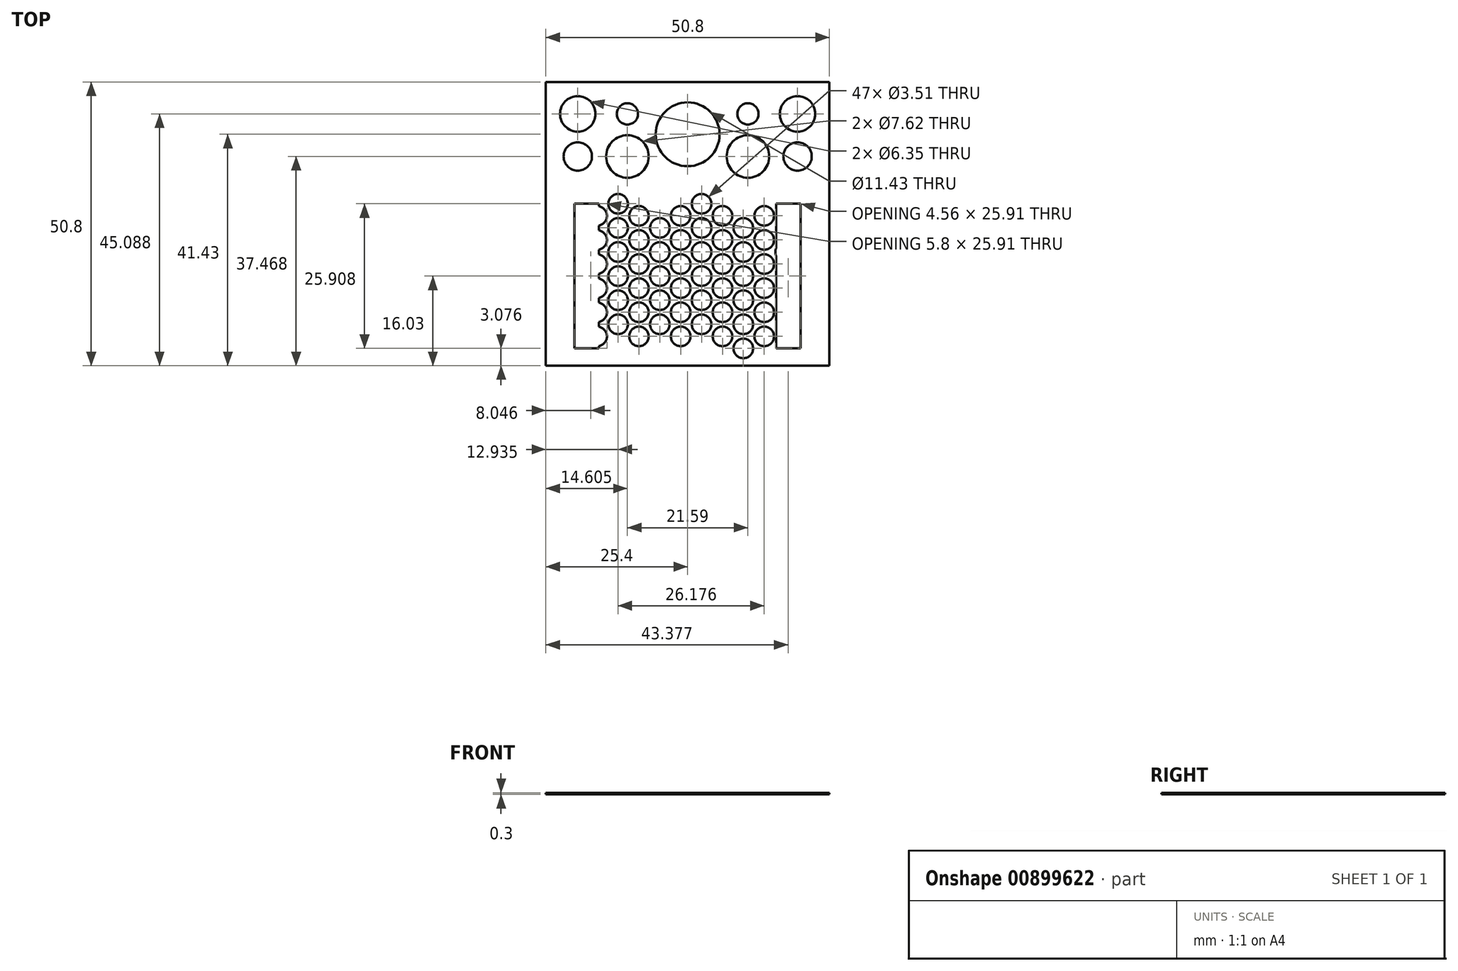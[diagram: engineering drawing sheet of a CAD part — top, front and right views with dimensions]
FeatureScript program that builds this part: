
annotation { "Feature Type Name" : "Feature", "Feature Type Description" : "" }
export const myFeature = defineFeature(function(context is Context, id is Id, definition is map)
    precondition{}
    {
        {
            var Q0;
            Q0=qCreatedBy(makeId("Top.planeOp"),FACE);
            var sketch = newSketch(context, id + "F0", { "sketchPlane" : qUnion([Q0])});
            skLineSegment(sketch, "E0.bottom", {"start": v(-25.4, -16.03) * mm, "end": v(25.4, -16.03) * mm});
            skLineSegment(sketch, "E0.top", {"start": v(-25.4, 34.77) * mm, "end": v(25.4, 34.77) * mm});
            skLineSegment(sketch, "E0.left", {"start": v(-25.4, -16.03) * mm, "end": v(-25.4, 34.77) * mm});
            skLineSegment(sketch, "E0.right", {"start": v(25.4, -16.03) * mm, "end": v(25.4, 34.77) * mm});
            skLineSegment(sketch, "E1.bottom", {"start": v(-20.26, -12.95) * mm, "end": v(20.26, -12.95) * mm});
            skLineSegment(sketch, "E1.top", {"start": v(-20.26, 12.95) * mm, "end": v(20.26, 12.95) * mm});
            skLineSegment(sketch, "E1.left", {"start": v(-20.26, -12.95) * mm, "end": v(-20.26, 12.95) * mm});
            skLineSegment(sketch, "E1.right", {"start": v(20.26, -12.95) * mm, "end": v(20.26, 12.95) * mm});
            skLineSegment(sketch, "E2", {"start": v(-15.88, 12.95) * mm, "end": v(-15.88, -12.95) * mm});
            skLineSegment(sketch, "E3", {"start": v(-20.26, -12.95) * mm, "end": v(20.26, 12.95) * mm, "construction": true});
            skLineSegment(sketch, "E4", {"start": v(15.88, -12.95) * mm, "end": v(15.88, 12.95) * mm});
            skCircle(sketch, "E5", {"center": v(-12.46, -8.64) * mm, "radius": 1.75 * mm});
            skCircle(sketch, "E6.cCircle", {"center": v(-12.46, -8.64) * mm, "radius": 3.74 * mm, "construction": true});
            skLineSegment(sketch, "E6.0", {"start": v(-8.73, -10.8) * mm, "end": v(-8.73, -6.48) * mm, "construction": true});
            skLineSegment(sketch, "E6.1", {"start": v(-12.46, -12.95) * mm, "end": v(-8.73, -10.8) * mm, "construction": true});
            skLineSegment(sketch, "E6.2", {"start": v(-16.2, -10.8) * mm, "end": v(-12.46, -12.95) * mm, "construction": true});
            skLineSegment(sketch, "E6.3", {"start": v(-16.2, -6.48) * mm, "end": v(-16.2, -10.8) * mm, "construction": true});
            skLineSegment(sketch, "E6.4", {"start": v(-12.46, -4.32) * mm, "end": v(-16.2, -6.48) * mm, "construction": true});
            skLineSegment(sketch, "E6.5", {"start": v(-8.73, -6.48) * mm, "end": v(-12.46, -4.32) * mm, "construction": true});
            skPoint(sketch, "E6.0.midPoint", {"position": v(-8.73, -8.64) * mm});
            skCircle(sketch, "E7", {"center": v(-16.2, -10.8) * mm, "radius": 1.75 * mm});
            skCircle(sketch, "E8", {"center": v(-16.2, -6.48) * mm, "radius": 1.75 * mm});
            skCircle(sketch, "E9", {"center": v(-12.46, -4.32) * mm, "radius": 1.75 * mm});
            skCircle(sketch, "E10.0.1.0", {"center": v(-16.2, -2.16) * mm, "radius": 1.75 * mm});
            skCircle(sketch, "E10.0.1.1", {"center": v(-12.46, 4.32) * mm, "radius": 1.75 * mm});
            skCircle(sketch, "E10.0.1.2", {"center": v(-16.2, 2.16) * mm, "radius": 1.75 * mm});
            skCircle(sketch, "E10.0.1.3", {"center": v(-12.46, 0) * mm, "radius": 1.75 * mm});
            skCircle(sketch, "E10.0.2.0", {"center": v(-16.2, 6.48) * mm, "radius": 1.75 * mm});
            skCircle(sketch, "E10.0.2.1", {"center": v(-12.46, 12.95) * mm, "radius": 1.75 * mm});
            skCircle(sketch, "E10.0.2.2", {"center": v(-16.2, 10.8) * mm, "radius": 1.75 * mm});
            skCircle(sketch, "E10.0.2.3", {"center": v(-12.46, 8.64) * mm, "radius": 1.75 * mm});
            skCircle(sketch, "E10.1.0.0", {"center": v(-8.73, -10.8) * mm, "radius": 1.75 * mm});
            skCircle(sketch, "E10.1.0.1", {"center": v(-4.99, -4.32) * mm, "radius": 1.75 * mm});
            skCircle(sketch, "E10.1.0.2", {"center": v(-8.73, -6.48) * mm, "radius": 1.75 * mm});
            skCircle(sketch, "E10.1.0.3", {"center": v(-4.99, -8.64) * mm, "radius": 1.75 * mm});
            skCircle(sketch, "E10.1.1.0", {"center": v(-8.73, -2.16) * mm, "radius": 1.75 * mm});
            skCircle(sketch, "E10.1.1.1", {"center": v(-4.99, 4.32) * mm, "radius": 1.75 * mm});
            skCircle(sketch, "E10.1.1.2", {"center": v(-8.73, 2.16) * mm, "radius": 1.75 * mm});
            skCircle(sketch, "E10.1.1.3", {"center": v(-4.99, 0) * mm, "radius": 1.75 * mm});
            skCircle(sketch, "E10.1.2.0", {"center": v(-8.73, 6.48) * mm, "radius": 1.75 * mm});
            skCircle(sketch, "E10.1.2.1", {"center": v(-4.99, 12.95) * mm, "radius": 1.75 * mm});
            skCircle(sketch, "E10.1.2.2", {"center": v(-8.73, 10.8) * mm, "radius": 1.75 * mm});
            skCircle(sketch, "E10.1.2.3", {"center": v(-4.99, 8.64) * mm, "radius": 1.75 * mm});
            skCircle(sketch, "E10.2.0.0", {"center": v(-1.25, -10.8) * mm, "radius": 1.75 * mm});
            skCircle(sketch, "E10.2.0.1", {"center": v(2.5, -4.32) * mm, "radius": 1.75 * mm});
            skCircle(sketch, "E10.2.0.2", {"center": v(-1.25, -6.48) * mm, "radius": 1.75 * mm});
            skCircle(sketch, "E10.2.0.3", {"center": v(2.5, -8.64) * mm, "radius": 1.75 * mm});
            skCircle(sketch, "E10.2.1.0", {"center": v(-1.25, -2.16) * mm, "radius": 1.75 * mm});
            skCircle(sketch, "E10.2.1.1", {"center": v(2.5, 4.32) * mm, "radius": 1.75 * mm});
            skCircle(sketch, "E10.2.1.2", {"center": v(-1.25, 2.16) * mm, "radius": 1.75 * mm});
            skCircle(sketch, "E10.2.1.3", {"center": v(2.5, 0) * mm, "radius": 1.75 * mm});
            skCircle(sketch, "E10.2.2.0", {"center": v(-1.25, 6.48) * mm, "radius": 1.75 * mm});
            skCircle(sketch, "E10.2.2.1", {"center": v(2.5, 12.95) * mm, "radius": 1.75 * mm});
            skCircle(sketch, "E10.2.2.2", {"center": v(-1.25, 10.8) * mm, "radius": 1.75 * mm});
            skCircle(sketch, "E10.2.2.3", {"center": v(2.5, 8.64) * mm, "radius": 1.75 * mm});
            skCircle(sketch, "E10.3.0.0", {"center": v(6.23, -10.8) * mm, "radius": 1.75 * mm});
            skCircle(sketch, "E10.3.0.1", {"center": v(9.97, -4.32) * mm, "radius": 1.75 * mm});
            skCircle(sketch, "E10.3.0.2", {"center": v(6.23, -6.48) * mm, "radius": 1.75 * mm});
            skCircle(sketch, "E10.3.0.3", {"center": v(9.97, -8.64) * mm, "radius": 1.75 * mm});
            skCircle(sketch, "E10.3.1.0", {"center": v(6.23, -2.16) * mm, "radius": 1.75 * mm});
            skCircle(sketch, "E10.3.1.1", {"center": v(9.97, 4.32) * mm, "radius": 1.75 * mm});
            skCircle(sketch, "E10.3.1.2", {"center": v(6.23, 2.16) * mm, "radius": 1.75 * mm});
            skCircle(sketch, "E10.3.1.3", {"center": v(9.97, 0) * mm, "radius": 1.75 * mm});
            skCircle(sketch, "E10.3.2.0", {"center": v(6.23, 6.48) * mm, "radius": 1.75 * mm});
            skCircle(sketch, "E10.3.2.1", {"center": v(9.97, 12.95) * mm, "radius": 1.75 * mm});
            skCircle(sketch, "E10.3.2.2", {"center": v(6.23, 10.8) * mm, "radius": 1.75 * mm});
            skCircle(sketch, "E10.3.2.3", {"center": v(9.97, 8.64) * mm, "radius": 1.75 * mm});
            skLineSegment(sketch, "E10.direction1", {"start": v(-16.2, -10.8) * mm, "end": v(-8.73, -10.8) * mm, "construction": true});
            skLineSegment(sketch, "E10.direction2", {"start": v(-16.2, -10.8) * mm, "end": v(-16.2, -2.16) * mm, "construction": true});
            skLineSegment(sketch, "E11", {"start": v(-8.73, -6.48) * mm, "end": v(-8.73, -2.16) * mm, "construction": true});
            skLineSegment(sketch, "E12", {"start": v(-1.25, 2.16) * mm, "end": v(0, 0) * mm, "construction": true});
            skLineSegment(sketch, "E13", {"start": v(0, 0) * mm, "end": v(2.5, 0) * mm, "construction": true});
            skLineSegment(sketch, "E14", {"start": v(-1.25, -2.16) * mm, "end": v(0, 0) * mm, "construction": true});
            skCircle(sketch, "E15.0.4.0", {"center": v(13.71, -10.8) * mm, "radius": 1.75 * mm});
            skCircle(sketch, "E15.2.4.0", {"center": v(17.45, -4.32) * mm, "radius": 1.75 * mm});
            skCircle(sketch, "E15.4.4.0", {"center": v(13.71, -6.48) * mm, "radius": 1.75 * mm});
            skCircle(sketch, "E15.6.4.0", {"center": v(17.45, -8.64) * mm, "radius": 1.75 * mm});
            skCircle(sketch, "E15.0.4.1", {"center": v(13.71, -2.16) * mm, "radius": 1.75 * mm});
            skCircle(sketch, "E15.2.4.1", {"center": v(17.45, 4.32) * mm, "radius": 1.75 * mm});
            skCircle(sketch, "E15.4.4.1", {"center": v(13.71, 2.16) * mm, "radius": 1.75 * mm});
            skCircle(sketch, "E15.6.4.1", {"center": v(17.45, 0) * mm, "radius": 1.75 * mm});
            skCircle(sketch, "E15.0.4.2", {"center": v(13.71, 6.48) * mm, "radius": 1.75 * mm});
            skCircle(sketch, "E15.2.4.2", {"center": v(17.45, 12.95) * mm, "radius": 1.75 * mm});
            skCircle(sketch, "E15.4.4.2", {"center": v(13.71, 10.8) * mm, "radius": 1.75 * mm});
            skCircle(sketch, "E15.6.4.2", {"center": v(17.45, 8.64) * mm, "radius": 1.75 * mm});
            skCircle(sketch, "E16", {"center": v(-12.46, -12.95) * mm, "radius": 1.75 * mm});
            skCircle(sketch, "E17.1.0.0", {"center": v(-4.99, -12.95) * mm, "radius": 1.75 * mm});
            skCircle(sketch, "E17.2.0.0", {"center": v(2.5, -12.95) * mm, "radius": 1.75 * mm});
            skCircle(sketch, "E17.3.0.0", {"center": v(9.97, -12.95) * mm, "radius": 1.75 * mm});
            skLineSegment(sketch, "E17.direction1", {"start": v(-12.46, -12.95) * mm, "end": v(-4.99, -12.95) * mm, "construction": true});
            skLineSegment(sketch, "E18", {"start": v(-8.73, -10.8) * mm, "end": v(-4.99, -12.95) * mm, "construction": true});
            skLineSegment(sketch, "E19", {"start": v(-25.4, 16.03) * mm, "end": v(25.4, 16.03) * mm, "construction": true});
            skLineSegment(sketch, "E20", {"start": v(0, -16.03) * mm, "end": v(0, 0) * mm, "construction": true});
            skCircle(sketch, "E21.MirrorC", {"center": v(16.2, 6.48) * mm, "radius": 1.75 * mm, "construction": true});
            skCircle(sketch, "E22.MirrorC", {"center": v(-13.71, 6.48) * mm, "radius": 1.75 * mm, "construction": true});
            skCircle(sketch, "E23.MirrorC", {"center": v(12.46, 8.64) * mm, "radius": 1.75 * mm, "construction": true});
            skCircle(sketch, "E24.MirrorC", {"center": v(16.2, 10.8) * mm, "radius": 1.75 * mm, "construction": true});
            skCircle(sketch, "E25", {"center": v(0, 25.4) * mm, "radius": 5.72 * mm});
            skCircle(sketch, "E26", {"center": v(10.8, 21.44) * mm, "radius": 3.81 * mm});
            skCircle(sketch, "E27", {"center": v(19.69, 21.44) * mm, "radius": 2.54 * mm});
            skCircle(sketch, "E28", {"center": v(19.69, 29.06) * mm, "radius": 3.18 * mm});
            skCircle(sketch, "E29", {"center": v(10.8, 29.06) * mm, "radius": 1.9 * mm});
            skLineSegment(sketch, "E30", {"start": v(0, 16.03) * mm, "end": v(0, 34.77) * mm, "construction": true});
            skLineSegment(sketch, "E31", {"start": v(10.8, 29.06) * mm, "end": v(19.69, 29.06) * mm, "construction": true});
            skLineSegment(sketch, "E32", {"start": v(19.69, 29.06) * mm, "end": v(19.69, 21.44) * mm, "construction": true});
            skLineSegment(sketch, "E33", {"start": v(10.8, 29.06) * mm, "end": v(10.8, 21.44) * mm, "construction": true});
            skLineSegment(sketch, "E34", {"start": v(19.69, 21.44) * mm, "end": v(10.8, 21.44) * mm, "construction": true});
            skCircle(sketch, "E35.MirrorC", {"center": v(-19.69, 21.44) * mm, "radius": 2.54 * mm});
            skCircle(sketch, "E36.MirrorC", {"center": v(-10.8, 29.06) * mm, "radius": 1.9 * mm});
            skCircle(sketch, "E37.MirrorC", {"center": v(-19.69, 29.06) * mm, "radius": 3.18 * mm});
            skCircle(sketch, "E38.MirrorC", {"center": v(-10.8, 21.44) * mm, "radius": 3.81 * mm});
            skSolve(sketch);
        }
        {
            var Q0;
            Q0=makeQuery(id+"F0.imprint","IMPRINT",FACE,{"disambiguationData":[TD([[makeQuery(id+"F0.imprint","IMPRINT",EDGE,{"derivedFrom":sQuery(id+"F0.wireOp",EDGE,"E0.bottom")}),1.0]])]});
            var Q1;
            {var subQ44=sQuery(id+"F0.wireOp",EDGE,"t1qjbQJ7-sn4I-aTcP-LZPk-unipsoKl5fNM");Q1=makeQuery(id+"F0.imprint","IMPRINT",FACE,{"disambiguationData":[TD([[makeQuery(id+"F0.imprint","IMPRINT",EDGE,{"derivedFrom":subQ44}),-1.0]])]});}
            var Q2;
            {var subQ0=sQuery(id+"F0.wireOp",EDGE,"8adf1148-75b4-4e6a-bf28-ab6f81f17e44.3.0.0");var subQ1=sQuery(id+"F0.wireOp",EDGE,"E1.top");var subQ2=makeQuery(id+"F0.imprint","INTERSECT",VERTEX,{"disambiguationData":[OD(0.0)],"derivedFrom":[subQ1,subQ0]});Q2=makeQuery(id+"F0.imprint","IMPRINT",FACE,{"disambiguationData":[TD([[makeQuery(id+"F0.imprint","IMPRINT",EDGE,{"disambiguationData":[TD([[subQ2,-1.0]])],"derivedFrom":subQ1}),1.0]])]});}
            var Q3;
            {var subQ0=sQuery(id+"F0.wireOp",EDGE,"8adf1148-75b4-4e6a-bf28-ab6f81f17e44.3.0.1");var subQ1=sQuery(id+"F0.wireOp",EDGE,"E1.top");var subQ2=makeQuery(id+"F0.imprint","INTERSECT",VERTEX,{"disambiguationData":[OD(0.0)],"derivedFrom":[subQ1,subQ0]});Q3=makeQuery(id+"F0.imprint","IMPRINT",FACE,{"disambiguationData":[TD([[makeQuery(id+"F0.imprint","IMPRINT",EDGE,{"disambiguationData":[TD([[subQ2,-1.0]])],"derivedFrom":subQ1}),1.0]])]});}
            var Q4;
            {var subQ0=sQuery(id+"F0.wireOp",EDGE,"8adf1148-75b4-4e6a-bf28-ab6f81f17e44.3.0.2");var subQ1=sQuery(id+"F0.wireOp",EDGE,"E1.top");var subQ2=makeQuery(id+"F0.imprint","INTERSECT",VERTEX,{"disambiguationData":[OD(0.0)],"derivedFrom":[subQ1,subQ0]});Q4=makeQuery(id+"F0.imprint","IMPRINT",FACE,{"disambiguationData":[TD([[makeQuery(id+"F0.imprint","IMPRINT",EDGE,{"disambiguationData":[TD([[subQ2,-1.0]])],"derivedFrom":subQ1}),1.0]])]});}
            var Q5;
            {var subQ0=sQuery(id+"F0.wireOp",EDGE,"8adf1148-75b4-4e6a-bf28-ab6f81f17e44.3.0.3");var subQ1=sQuery(id+"F0.wireOp",EDGE,"E1.top");var subQ2=makeQuery(id+"F0.imprint","INTERSECT",VERTEX,{"disambiguationData":[OD(0.0)],"derivedFrom":[subQ1,subQ0]});Q5=makeQuery(id+"F0.imprint","IMPRINT",FACE,{"disambiguationData":[TD([[makeQuery(id+"F0.imprint","IMPRINT",EDGE,{"disambiguationData":[TD([[subQ2,-1.0]])],"derivedFrom":subQ1}),1.0]])]});}
            var Q6;
            {var subQ0=sQuery(id+"F0.wireOp",EDGE,"8adf1148-75b4-4e6a-bf28-ab6f81f17e44.3.0.4");var subQ1=sQuery(id+"F0.wireOp",EDGE,"E1.top");var subQ2=makeQuery(id+"F0.imprint","INTERSECT",VERTEX,{"disambiguationData":[OD(0.0)],"derivedFrom":[subQ1,subQ0]});Q6=makeQuery(id+"F0.imprint","IMPRINT",FACE,{"disambiguationData":[TD([[makeQuery(id+"F0.imprint","IMPRINT",EDGE,{"disambiguationData":[TD([[subQ2,-1.0]])],"derivedFrom":subQ1}),1.0]])]});}
            var Q7;
            {var subQ0=sQuery(id+"F0.wireOp",EDGE,"8adf1148-75b4-4e6a-bf28-ab6f81f17e44.3.0.5");var subQ1=sQuery(id+"F0.wireOp",EDGE,"E1.top");var subQ2=makeQuery(id+"F0.imprint","INTERSECT",VERTEX,{"disambiguationData":[OD(0.0)],"derivedFrom":[subQ1,subQ0]});Q7=makeQuery(id+"F0.imprint","IMPRINT",FACE,{"disambiguationData":[TD([[makeQuery(id+"F0.imprint","IMPRINT",EDGE,{"disambiguationData":[TD([[subQ2,-1.0]])],"derivedFrom":subQ1}),1.0]])]});}
            var Q8;
            {var subQ0=sQuery(id+"F0.wireOp",EDGE,"8adf1148-75b4-4e6a-bf28-ab6f81f17e44.3.0.6");var subQ1=sQuery(id+"F0.wireOp",EDGE,"E1.top");var subQ2=makeQuery(id+"F0.imprint","INTERSECT",VERTEX,{"disambiguationData":[OD(0.0)],"derivedFrom":[subQ1,subQ0]});Q8=makeQuery(id+"F0.imprint","IMPRINT",FACE,{"disambiguationData":[TD([[makeQuery(id+"F0.imprint","IMPRINT",EDGE,{"disambiguationData":[TD([[subQ2,-1.0]])],"derivedFrom":subQ1}),1.0]])]});}
            var Q9;
            {var subQ0=sQuery(id+"F0.wireOp",EDGE,"8adf1148-75b4-4e6a-bf28-ab6f81f17e44.3.0.7");var subQ1=sQuery(id+"F0.wireOp",EDGE,"E1.top");var subQ2=makeQuery(id+"F0.imprint","INTERSECT",VERTEX,{"disambiguationData":[OD(0.0)],"derivedFrom":[subQ1,subQ0]});Q9=makeQuery(id+"F0.imprint","IMPRINT",FACE,{"disambiguationData":[TD([[makeQuery(id+"F0.imprint","IMPRINT",EDGE,{"disambiguationData":[TD([[subQ2,-1.0]])],"derivedFrom":subQ1}),1.0]])]});}
            var Q10;
            {var subQ0=sQuery(id+"F0.wireOp",EDGE,"E1.bottom");var subQ1=makeQuery(id+"F0.imprint","INTERSECT",VERTEX,{"derivedFrom":[subQ0,sQuery(id+"F0.wireOp",EDGE,"E2")]});Q10=makeQuery(id+"F0.imprint","IMPRINT",FACE,{"disambiguationData":[TD([[makeQuery(id+"F0.imprint","IMPRINT",EDGE,{"disambiguationData":[TD([[subQ1,1.0]])],"derivedFrom":subQ0}),-1.0]])]});}
            var Q11;
            {var subQ0=sQuery(id+"F0.wireOp",EDGE,"4aa1bb0b-9ea2-492a-a7d2-e5d0de5c6c84.2.0.0");var subQ1=sQuery(id+"F0.wireOp",EDGE,"E1.bottom");var subQ2=makeQuery(id+"F0.imprint","INTERSECT",VERTEX,{"disambiguationData":[OD(0.0)],"derivedFrom":[subQ1,subQ0]});Q11=makeQuery(id+"F0.imprint","IMPRINT",FACE,{"disambiguationData":[TD([[makeQuery(id+"F0.imprint","IMPRINT",EDGE,{"disambiguationData":[TD([[subQ2,-1.0]])],"derivedFrom":subQ1}),-1.0]])]});}
            var Q12;
            {var subQ0=sQuery(id+"F0.wireOp",EDGE,"4aa1bb0b-9ea2-492a-a7d2-e5d0de5c6c84.3.0.0");var subQ1=sQuery(id+"F0.wireOp",EDGE,"E1.bottom");var subQ2=makeQuery(id+"F0.imprint","INTERSECT",VERTEX,{"disambiguationData":[OD(0.0)],"derivedFrom":[subQ1,subQ0]});Q12=makeQuery(id+"F0.imprint","IMPRINT",FACE,{"disambiguationData":[TD([[makeQuery(id+"F0.imprint","IMPRINT",EDGE,{"disambiguationData":[TD([[subQ2,-1.0]])],"derivedFrom":subQ1}),-1.0]])]});}
            var Q13;
            {var subQ0=sQuery(id+"F0.wireOp",EDGE,"4aa1bb0b-9ea2-492a-a7d2-e5d0de5c6c84.4.0.0");var subQ1=sQuery(id+"F0.wireOp",EDGE,"E1.bottom");var subQ2=makeQuery(id+"F0.imprint","INTERSECT",VERTEX,{"disambiguationData":[OD(0.0)],"derivedFrom":[subQ1,subQ0]});Q13=makeQuery(id+"F0.imprint","IMPRINT",FACE,{"disambiguationData":[TD([[makeQuery(id+"F0.imprint","IMPRINT",EDGE,{"disambiguationData":[TD([[subQ2,-1.0]])],"derivedFrom":subQ1}),-1.0]])]});}
            var Q14;
            {var subQ0=sQuery(id+"F0.wireOp",EDGE,"4aa1bb0b-9ea2-492a-a7d2-e5d0de5c6c84.5.0.0");var subQ1=sQuery(id+"F0.wireOp",EDGE,"E1.bottom");var subQ2=makeQuery(id+"F0.imprint","INTERSECT",VERTEX,{"disambiguationData":[OD(0.0)],"derivedFrom":[subQ1,subQ0]});Q14=makeQuery(id+"F0.imprint","IMPRINT",FACE,{"disambiguationData":[TD([[makeQuery(id+"F0.imprint","IMPRINT",EDGE,{"disambiguationData":[TD([[subQ2,-1.0]])],"derivedFrom":subQ1}),-1.0]])]});}
            var Q15;
            {var subQ0=sQuery(id+"F0.wireOp",EDGE,"4aa1bb0b-9ea2-492a-a7d2-e5d0de5c6c84.6.0.0");var subQ1=sQuery(id+"F0.wireOp",EDGE,"E1.bottom");var subQ2=makeQuery(id+"F0.imprint","INTERSECT",VERTEX,{"disambiguationData":[OD(0.0)],"derivedFrom":[subQ1,subQ0]});Q15=makeQuery(id+"F0.imprint","IMPRINT",FACE,{"disambiguationData":[TD([[makeQuery(id+"F0.imprint","IMPRINT",EDGE,{"disambiguationData":[TD([[subQ2,-1.0]])],"derivedFrom":subQ1}),-1.0]])]});}
            var Q16;
            {var subQ0=sQuery(id+"F0.wireOp",EDGE,"E1.bottom");var subQ1=makeQuery(id+"F0.imprint","INTERSECT",VERTEX,{"derivedFrom":[subQ0,sQuery(id+"F0.wireOp",EDGE,"lBorHLWZ-BlnR-iAhn-TYBT-jcVwYFToGvxp")]});Q16=makeQuery(id+"F0.imprint","IMPRINT",FACE,{"disambiguationData":[TD([[makeQuery(id+"F0.imprint","IMPRINT",EDGE,{"disambiguationData":[TD([[subQ1,1.0]])],"derivedFrom":subQ0}),-1.0]])]});}
            var Q17;
            {var subQ0=sQuery(id+"F0.wireOp",EDGE,"4aa1bb0b-9ea2-492a-a7d2-e5d0de5c6c84.1.0.0");var subQ1=sQuery(id+"F0.wireOp",EDGE,"E1.bottom");var subQ2=makeQuery(id+"F0.imprint","INTERSECT",VERTEX,{"disambiguationData":[OD(0.0)],"derivedFrom":[subQ1,subQ0]});Q17=makeQuery(id+"F0.imprint","IMPRINT",FACE,{"disambiguationData":[TD([[makeQuery(id+"F0.imprint","IMPRINT",EDGE,{"disambiguationData":[TD([[subQ2,-1.0]])],"derivedFrom":subQ1}),-1.0]])]});}
            var Q18;
            {var subQ0=sQuery(id+"F0.wireOp",EDGE,"t1qjbQJ7-sn4I-aTcP-LZPk-unipsoKl5fNM");var subQ1=sQuery(id+"F0.wireOp",EDGE,"E1.bottom");var subQ2=makeQuery(id+"F0.imprint","INTERSECT",VERTEX,{"disambiguationData":[OD(0.0)],"derivedFrom":[subQ1,subQ0]});Q18=makeQuery(id+"F0.imprint","IMPRINT",FACE,{"disambiguationData":[TD([[makeQuery(id+"F0.imprint","IMPRINT",EDGE,{"disambiguationData":[TD([[subQ2,-1.0]])],"derivedFrom":subQ1}),-1.0]])]});}
            var Q19;
            Q19=makeQuery(id+"F0.imprint","IMPRINT",FACE,{"disambiguationData":[TD([[makeQuery(id+"F0.imprint","IMPRINT",EDGE,{"derivedFrom":sQuery(id+"F0.wireOp",EDGE,"PQAykTsZ-QeuR-cZSH-uwzk-X1mISoGLeRIY")}),-1.0]])]});
            var Q20;
            {var subQ0=sQuery(id+"F0.wireOp",EDGE,"E1.top");var subQ1=makeQuery(id+"F0.imprint","INTERSECT",VERTEX,{"derivedFrom":[subQ0,sQuery(id+"F0.wireOp",EDGE,"E2")]});Q20=makeQuery(id+"F0.imprint","IMPRINT",FACE,{"disambiguationData":[TD([[makeQuery(id+"F0.imprint","IMPRINT",EDGE,{"disambiguationData":[TD([[subQ1,1.0]])],"derivedFrom":subQ0}),1.0]])]});}
            var Q21;
            {var subQ0=sQuery(id+"F0.wireOp",EDGE,"532b062d-e405-47f6-8b05-6f6e2308ab52.3.0.1");var subQ1=sQuery(id+"F0.wireOp",EDGE,"E1.top");var subQ2=makeQuery(id+"F0.imprint","INTERSECT",VERTEX,{"disambiguationData":[OD(0.0)],"derivedFrom":[subQ1,subQ0]});Q21=makeQuery(id+"F0.imprint","IMPRINT",FACE,{"disambiguationData":[TD([[makeQuery(id+"F0.imprint","IMPRINT",EDGE,{"disambiguationData":[TD([[subQ2,-1.0]])],"derivedFrom":subQ1}),1.0]])]});}
            var Q22;
            {var subQ0=sQuery(id+"F0.wireOp",EDGE,"532b062d-e405-47f6-8b05-6f6e2308ab52.3.0.2");var subQ1=sQuery(id+"F0.wireOp",EDGE,"E1.top");var subQ2=makeQuery(id+"F0.imprint","INTERSECT",VERTEX,{"disambiguationData":[OD(0.0)],"derivedFrom":[subQ1,subQ0]});Q22=makeQuery(id+"F0.imprint","IMPRINT",FACE,{"disambiguationData":[TD([[makeQuery(id+"F0.imprint","IMPRINT",EDGE,{"disambiguationData":[TD([[subQ2,-1.0]])],"derivedFrom":subQ1}),1.0]])]});}
            var Q23;
            {var subQ0=sQuery(id+"F0.wireOp",EDGE,"532b062d-e405-47f6-8b05-6f6e2308ab52.3.0.3");var subQ1=sQuery(id+"F0.wireOp",EDGE,"E1.top");var subQ2=makeQuery(id+"F0.imprint","INTERSECT",VERTEX,{"disambiguationData":[OD(0.0)],"derivedFrom":[subQ1,subQ0]});Q23=makeQuery(id+"F0.imprint","IMPRINT",FACE,{"disambiguationData":[TD([[makeQuery(id+"F0.imprint","IMPRINT",EDGE,{"disambiguationData":[TD([[subQ2,-1.0]])],"derivedFrom":subQ1}),1.0]])]});}
            var Q24;
            {var subQ0=sQuery(id+"F0.wireOp",EDGE,"532b062d-e405-47f6-8b05-6f6e2308ab52.3.0.4");var subQ1=sQuery(id+"F0.wireOp",EDGE,"E1.top");var subQ2=makeQuery(id+"F0.imprint","INTERSECT",VERTEX,{"disambiguationData":[OD(0.0)],"derivedFrom":[subQ1,subQ0]});Q24=makeQuery(id+"F0.imprint","IMPRINT",FACE,{"disambiguationData":[TD([[makeQuery(id+"F0.imprint","IMPRINT",EDGE,{"disambiguationData":[TD([[subQ2,-1.0]])],"derivedFrom":subQ1}),1.0]])]});}
            var Q25;
            {var subQ0=sQuery(id+"F0.wireOp",EDGE,"532b062d-e405-47f6-8b05-6f6e2308ab52.3.0.5");var subQ1=sQuery(id+"F0.wireOp",EDGE,"E1.top");var subQ2=makeQuery(id+"F0.imprint","INTERSECT",VERTEX,{"disambiguationData":[OD(0.0)],"derivedFrom":[subQ1,subQ0]});Q25=makeQuery(id+"F0.imprint","IMPRINT",FACE,{"disambiguationData":[TD([[makeQuery(id+"F0.imprint","IMPRINT",EDGE,{"disambiguationData":[TD([[subQ2,-1.0]])],"derivedFrom":subQ1}),1.0]])]});}
            var Q26;
            {var subQ0=sQuery(id+"F0.wireOp",EDGE,"532b062d-e405-47f6-8b05-6f6e2308ab52.3.0.6");var subQ1=sQuery(id+"F0.wireOp",EDGE,"E1.top");var subQ2=makeQuery(id+"F0.imprint","INTERSECT",VERTEX,{"disambiguationData":[OD(0.0)],"derivedFrom":[subQ1,subQ0]});Q26=makeQuery(id+"F0.imprint","IMPRINT",FACE,{"disambiguationData":[TD([[makeQuery(id+"F0.imprint","IMPRINT",EDGE,{"disambiguationData":[TD([[subQ2,-1.0]])],"derivedFrom":subQ1}),1.0]])]});}
            var Q27;
            {var subQ0=sQuery(id+"F0.wireOp",EDGE,"E1.top");var subQ1=makeQuery(id+"F0.imprint","INTERSECT",VERTEX,{"derivedFrom":[subQ0,sQuery(id+"F0.wireOp",EDGE,"lBorHLWZ-BlnR-iAhn-TYBT-jcVwYFToGvxp")]});Q27=makeQuery(id+"F0.imprint","IMPRINT",FACE,{"disambiguationData":[TD([[makeQuery(id+"F0.imprint","IMPRINT",EDGE,{"disambiguationData":[TD([[subQ1,1.0]])],"derivedFrom":subQ0}),1.0]])]});}
            var Q28;
            {var subQ0=sQuery(id+"F0.wireOp",EDGE,"E10.0.2.1");var subQ1=sQuery(id+"F0.wireOp",EDGE,"E1.top");var subQ2=makeQuery(id+"F0.imprint","INTERSECT",VERTEX,{"disambiguationData":[OD(0.0)],"derivedFrom":[subQ1,subQ0]});Q28=makeQuery(id+"F0.imprint","IMPRINT",FACE,{"disambiguationData":[TD([[makeQuery(id+"F0.imprint","IMPRINT",EDGE,{"disambiguationData":[TD([[subQ2,-1.0]])],"derivedFrom":subQ1}),1.0]])]});}
            var Q29;
            {var subQ0=sQuery(id+"F0.wireOp",EDGE,"E10.1.2.1");var subQ1=sQuery(id+"F0.wireOp",EDGE,"E1.top");var subQ2=makeQuery(id+"F0.imprint","INTERSECT",VERTEX,{"disambiguationData":[OD(0.0)],"derivedFrom":[subQ1,subQ0]});Q29=makeQuery(id+"F0.imprint","IMPRINT",FACE,{"disambiguationData":[TD([[makeQuery(id+"F0.imprint","IMPRINT",EDGE,{"disambiguationData":[TD([[subQ2,-1.0]])],"derivedFrom":subQ1}),1.0]])]});}
            var Q30;
            {var subQ0=sQuery(id+"F0.wireOp",EDGE,"E10.2.2.1");var subQ1=sQuery(id+"F0.wireOp",EDGE,"E1.top");var subQ2=makeQuery(id+"F0.imprint","INTERSECT",VERTEX,{"disambiguationData":[OD(0.0)],"derivedFrom":[subQ1,subQ0]});Q30=makeQuery(id+"F0.imprint","IMPRINT",FACE,{"disambiguationData":[TD([[makeQuery(id+"F0.imprint","IMPRINT",EDGE,{"disambiguationData":[TD([[subQ2,-1.0]])],"derivedFrom":subQ1}),1.0]])]});}
            var Q31;
            {var subQ0=sQuery(id+"F0.wireOp",EDGE,"E17.1.0.0");var subQ1=sQuery(id+"F0.wireOp",EDGE,"E1.bottom");var subQ2=makeQuery(id+"F0.imprint","INTERSECT",VERTEX,{"disambiguationData":[OD(0.0)],"derivedFrom":[subQ1,subQ0]});Q31=makeQuery(id+"F0.imprint","IMPRINT",FACE,{"disambiguationData":[TD([[makeQuery(id+"F0.imprint","IMPRINT",EDGE,{"disambiguationData":[TD([[subQ2,-1.0]])],"derivedFrom":subQ1}),-1.0]])]});}
            var Q32;
            {var subQ0=sQuery(id+"F0.wireOp",EDGE,"E17.2.0.0");var subQ1=sQuery(id+"F0.wireOp",EDGE,"E1.bottom");var subQ2=makeQuery(id+"F0.imprint","INTERSECT",VERTEX,{"disambiguationData":[OD(0.0)],"derivedFrom":[subQ1,subQ0]});Q32=makeQuery(id+"F0.imprint","IMPRINT",FACE,{"disambiguationData":[TD([[makeQuery(id+"F0.imprint","IMPRINT",EDGE,{"disambiguationData":[TD([[subQ2,-1.0]])],"derivedFrom":subQ1}),-1.0]])]});}
            var Q33;
            {var subQ0=sQuery(id+"F0.wireOp",EDGE,"E17.3.0.0");var subQ1=sQuery(id+"F0.wireOp",EDGE,"E1.bottom");var subQ2=makeQuery(id+"F0.imprint","INTERSECT",VERTEX,{"disambiguationData":[OD(0.0)],"derivedFrom":[subQ1,subQ0]});Q33=makeQuery(id+"F0.imprint","IMPRINT",FACE,{"disambiguationData":[TD([[makeQuery(id+"F0.imprint","IMPRINT",EDGE,{"disambiguationData":[TD([[subQ2,-1.0]])],"derivedFrom":subQ1}),-1.0]])]});}
            var Q34;
            {var subQ0=sQuery(id+"F0.wireOp",EDGE,"E10.3.2.1");var subQ1=sQuery(id+"F0.wireOp",EDGE,"E1.top");var subQ2=makeQuery(id+"F0.imprint","INTERSECT",VERTEX,{"disambiguationData":[OD(0.0)],"derivedFrom":[subQ1,subQ0]});Q34=makeQuery(id+"F0.imprint","IMPRINT",FACE,{"disambiguationData":[TD([[makeQuery(id+"F0.imprint","IMPRINT",EDGE,{"disambiguationData":[TD([[subQ2,-1.0]])],"derivedFrom":subQ1}),1.0]])]});}
            var Q35;
            {var subQ0=sQuery(id+"F0.wireOp",EDGE,"E16");var subQ1=sQuery(id+"F0.wireOp",EDGE,"E1.bottom");var subQ2=makeQuery(id+"F0.imprint","INTERSECT",VERTEX,{"disambiguationData":[OD(0.0)],"derivedFrom":[subQ1,subQ0]});Q35=makeQuery(id+"F0.imprint","IMPRINT",FACE,{"disambiguationData":[TD([[makeQuery(id+"F0.imprint","IMPRINT",EDGE,{"disambiguationData":[TD([[subQ2,-1.0]])],"derivedFrom":subQ1}),-1.0]])]});}
            var Q36;
            Q36=makeQuery(id+"F0.imprint","IMPRINT",FACE,{"disambiguationData":[TD([[makeQuery(id+"F0.imprint","IMPRINT",EDGE,{"derivedFrom":sQuery(id+"F0.wireOp",EDGE,"E5")}),-1.0]])]});
            var Q37;
            {var subQ0=sQuery(id+"F0.wireOp",EDGE,"E15.2.4.2");var subQ1=sQuery(id+"F0.wireOp",EDGE,"E1.top");var subQ2=makeQuery(id+"F0.imprint","INTERSECT",VERTEX,{"disambiguationData":[OD(0.0)],"derivedFrom":[subQ1,subQ0]});Q37=makeQuery(id+"F0.imprint","IMPRINT",FACE,{"disambiguationData":[TD([[makeQuery(id+"F0.imprint","IMPRINT",EDGE,{"disambiguationData":[TD([[subQ2,-1.0]])],"derivedFrom":subQ1}),1.0]])]});}
            var Q38;
            {var subQ0=sQuery(id+"F0.wireOp",EDGE,"E15.2.4.0");var subQ1=sQuery(id+"F0.wireOp",EDGE,"E4");var subQ2=makeQuery(id+"F0.imprint","INTERSECT",VERTEX,{"disambiguationData":[OD(0.0)],"derivedFrom":[subQ1,subQ0]});Q38=makeQuery(id+"F0.imprint","IMPRINT",FACE,{"disambiguationData":[TD([[makeQuery(id+"F0.imprint","IMPRINT",EDGE,{"disambiguationData":[TD([[subQ2,-1.0]])],"derivedFrom":subQ1}),1.0]])]});}
            var Q39;
            {var subQ0=sQuery(id+"F0.wireOp",EDGE,"E15.6.4.0");var subQ1=sQuery(id+"F0.wireOp",EDGE,"E4");var subQ2=makeQuery(id+"F0.imprint","INTERSECT",VERTEX,{"disambiguationData":[OD(0.0)],"derivedFrom":[subQ1,subQ0]});Q39=makeQuery(id+"F0.imprint","IMPRINT",FACE,{"disambiguationData":[TD([[makeQuery(id+"F0.imprint","IMPRINT",EDGE,{"disambiguationData":[TD([[subQ2,-1.0]])],"derivedFrom":subQ1}),1.0]])]});}
            var Q40;
            {var subQ0=sQuery(id+"F0.wireOp",EDGE,"E15.6.4.1");var subQ1=sQuery(id+"F0.wireOp",EDGE,"E4");var subQ2=makeQuery(id+"F0.imprint","INTERSECT",VERTEX,{"disambiguationData":[OD(0.0)],"derivedFrom":[subQ1,subQ0]});Q40=makeQuery(id+"F0.imprint","IMPRINT",FACE,{"disambiguationData":[TD([[makeQuery(id+"F0.imprint","IMPRINT",EDGE,{"disambiguationData":[TD([[subQ2,-1.0]])],"derivedFrom":subQ1}),1.0]])]});}
            var Q41;
            {var subQ0=sQuery(id+"F0.wireOp",EDGE,"E15.2.4.1");var subQ1=sQuery(id+"F0.wireOp",EDGE,"E4");var subQ2=makeQuery(id+"F0.imprint","INTERSECT",VERTEX,{"disambiguationData":[OD(0.0)],"derivedFrom":[subQ1,subQ0]});Q41=makeQuery(id+"F0.imprint","IMPRINT",FACE,{"disambiguationData":[TD([[makeQuery(id+"F0.imprint","IMPRINT",EDGE,{"disambiguationData":[TD([[subQ2,-1.0]])],"derivedFrom":subQ1}),1.0]])]});}
            var Q42;
            {var subQ0=sQuery(id+"F0.wireOp",EDGE,"E15.6.4.2");var subQ1=sQuery(id+"F0.wireOp",EDGE,"E4");var subQ2=makeQuery(id+"F0.imprint","INTERSECT",VERTEX,{"disambiguationData":[OD(0.0)],"derivedFrom":[subQ1,subQ0]});Q42=makeQuery(id+"F0.imprint","IMPRINT",FACE,{"disambiguationData":[TD([[makeQuery(id+"F0.imprint","IMPRINT",EDGE,{"disambiguationData":[TD([[subQ2,-1.0]])],"derivedFrom":subQ1}),1.0]])]});}
            var Q43;
            {var subQ0=sQuery(id+"F0.wireOp",EDGE,"E4");var subQ1=sQuery(id+"F0.wireOp",EDGE,"E1.top");var subQ2=makeQuery(id+"F0.imprint","INTERSECT",VERTEX,{"derivedFrom":[subQ1,subQ0]});Q43=makeQuery(id+"F0.imprint","IMPRINT",FACE,{"disambiguationData":[TD([[makeQuery(id+"F0.imprint","IMPRINT",EDGE,{"disambiguationData":[TD([[subQ2,1.0]])],"derivedFrom":subQ1}),-1.0]])]});}
            var Q44;
            {var subQ0=sQuery(id+"F0.wireOp",EDGE,"E10.0.2.1");var subQ1=sQuery(id+"F0.wireOp",EDGE,"E1.top");var subQ2=makeQuery(id+"F0.imprint","INTERSECT",VERTEX,{"disambiguationData":[OD(0.0)],"derivedFrom":[subQ1,subQ0]});Q44=makeQuery(id+"F0.imprint","IMPRINT",FACE,{"disambiguationData":[TD([[makeQuery(id+"F0.imprint","IMPRINT",EDGE,{"disambiguationData":[TD([[subQ2,-1.0]])],"derivedFrom":subQ1}),-1.0]])]});}
            var Q45;
            {var subQ0=sQuery(id+"F0.wireOp",EDGE,"E10.1.2.1");var subQ1=sQuery(id+"F0.wireOp",EDGE,"E1.top");var subQ2=makeQuery(id+"F0.imprint","INTERSECT",VERTEX,{"disambiguationData":[OD(0.0)],"derivedFrom":[subQ1,subQ0]});Q45=makeQuery(id+"F0.imprint","IMPRINT",FACE,{"disambiguationData":[TD([[makeQuery(id+"F0.imprint","IMPRINT",EDGE,{"disambiguationData":[TD([[subQ2,-1.0]])],"derivedFrom":subQ1}),-1.0]])]});}
            var Q46;
            {var subQ0=sQuery(id+"F0.wireOp",EDGE,"E10.2.2.1");var subQ1=sQuery(id+"F0.wireOp",EDGE,"E1.top");var subQ2=makeQuery(id+"F0.imprint","INTERSECT",VERTEX,{"disambiguationData":[OD(0.0)],"derivedFrom":[subQ1,subQ0]});Q46=makeQuery(id+"F0.imprint","IMPRINT",FACE,{"disambiguationData":[TD([[makeQuery(id+"F0.imprint","IMPRINT",EDGE,{"disambiguationData":[TD([[subQ2,-1.0]])],"derivedFrom":subQ1}),-1.0]])]});}
            var Q47;
            {var subQ0=sQuery(id+"F0.wireOp",EDGE,"E10.3.2.1");var subQ1=sQuery(id+"F0.wireOp",EDGE,"E1.top");var subQ2=makeQuery(id+"F0.imprint","INTERSECT",VERTEX,{"disambiguationData":[OD(0.0)],"derivedFrom":[subQ1,subQ0]});Q47=makeQuery(id+"F0.imprint","IMPRINT",FACE,{"disambiguationData":[TD([[makeQuery(id+"F0.imprint","IMPRINT",EDGE,{"disambiguationData":[TD([[subQ2,-1.0]])],"derivedFrom":subQ1}),-1.0]])]});}
            var Q48;
            {var subQ0=sQuery(id+"F0.wireOp",EDGE,"E17.3.0.0");var subQ1=sQuery(id+"F0.wireOp",EDGE,"E1.bottom");var subQ2=makeQuery(id+"F0.imprint","INTERSECT",VERTEX,{"disambiguationData":[OD(0.0)],"derivedFrom":[subQ1,subQ0]});Q48=makeQuery(id+"F0.imprint","IMPRINT",FACE,{"disambiguationData":[TD([[makeQuery(id+"F0.imprint","IMPRINT",EDGE,{"disambiguationData":[TD([[subQ2,-1.0]])],"derivedFrom":subQ1}),1.0]])]});}
            var Q49;
            {var subQ0=sQuery(id+"F0.wireOp",EDGE,"E17.2.0.0");var subQ1=sQuery(id+"F0.wireOp",EDGE,"E1.bottom");var subQ2=makeQuery(id+"F0.imprint","INTERSECT",VERTEX,{"disambiguationData":[OD(0.0)],"derivedFrom":[subQ1,subQ0]});Q49=makeQuery(id+"F0.imprint","IMPRINT",FACE,{"disambiguationData":[TD([[makeQuery(id+"F0.imprint","IMPRINT",EDGE,{"disambiguationData":[TD([[subQ2,-1.0]])],"derivedFrom":subQ1}),1.0]])]});}
            var Q50;
            {var subQ0=sQuery(id+"F0.wireOp",EDGE,"E17.1.0.0");var subQ1=sQuery(id+"F0.wireOp",EDGE,"E1.bottom");var subQ2=makeQuery(id+"F0.imprint","INTERSECT",VERTEX,{"disambiguationData":[OD(0.0)],"derivedFrom":[subQ1,subQ0]});Q50=makeQuery(id+"F0.imprint","IMPRINT",FACE,{"disambiguationData":[TD([[makeQuery(id+"F0.imprint","IMPRINT",EDGE,{"disambiguationData":[TD([[subQ2,-1.0]])],"derivedFrom":subQ1}),1.0]])]});}
            var Q51;
            {var subQ0=sQuery(id+"F0.wireOp",EDGE,"E16");var subQ1=sQuery(id+"F0.wireOp",EDGE,"E1.bottom");var subQ2=makeQuery(id+"F0.imprint","INTERSECT",VERTEX,{"disambiguationData":[OD(0.0)],"derivedFrom":[subQ1,subQ0]});Q51=makeQuery(id+"F0.imprint","IMPRINT",FACE,{"disambiguationData":[TD([[makeQuery(id+"F0.imprint","IMPRINT",EDGE,{"disambiguationData":[TD([[subQ2,-1.0]])],"derivedFrom":subQ1}),1.0]])]});}
            extrude(context, id + "F1", {"entities" : qUnion([Q0, Q1, Q2, Q3, Q4, Q5, Q6, Q7, Q8, Q9, Q10, Q11, Q12, Q13, Q14, Q15, Q16, Q17, Q18, Q19, Q20, Q21, Q22, Q23, Q24, Q25, Q26, Q27, Q28, Q29, Q30, Q31, Q32, Q33, Q34, Q35, Q36, Q37, Q38, Q39, Q40, Q41, Q42, Q43, Q44, Q45, Q46, Q47, Q48, Q49, Q50, Q51]), "depth" : 0.3 * mm, "offsetDistance" : 25.4 * mm});
        }
        {
            var Q0;
            Q0=makeQuery(id+"F0.imprint","IMPRINT",FACE,{"disambiguationData":[TD([[makeQuery(id+"F0.imprint","IMPRINT",EDGE,{"derivedFrom":sQuery(id+"F0.wireOp",EDGE,"E25")}),1.0]])]});
            var Q1;
            Q1=makeQuery(id+"F0.imprint","IMPRINT",FACE,{"disambiguationData":[TD([[makeQuery(id+"F0.imprint","IMPRINT",EDGE,{"derivedFrom":sQuery(id+"F0.wireOp",EDGE,"E26")}),1.0]])]});
            var Q2;
            Q2=makeQuery(id+"F0.imprint","IMPRINT",FACE,{"disambiguationData":[TD([[makeQuery(id+"F0.imprint","IMPRINT",EDGE,{"derivedFrom":sQuery(id+"F0.wireOp",EDGE,"E29")}),1.0]])]});
            var Q3;
            Q3=makeQuery(id+"F0.imprint","IMPRINT",FACE,{"disambiguationData":[TD([[makeQuery(id+"F0.imprint","IMPRINT",EDGE,{"derivedFrom":sQuery(id+"F0.wireOp",EDGE,"E28")}),1.0]])]});
            var Q4;
            Q4=makeQuery(id+"F0.imprint","IMPRINT",FACE,{"disambiguationData":[TD([[makeQuery(id+"F0.imprint","IMPRINT",EDGE,{"derivedFrom":sQuery(id+"F0.wireOp",EDGE,"E27")}),1.0]])]});
            var Q5;
            Q5=makeQuery(id+"F0.imprint","IMPRINT",FACE,{"disambiguationData":[TD([[makeQuery(id+"F0.imprint","IMPRINT",EDGE,{"derivedFrom":sQuery(id+"F0.wireOp",EDGE,"E10.1.2.0")}),1.0]])]});
            var Q6;
            {var subQ0=sQuery(id+"F0.wireOp",EDGE,"E10.1.2.1");var subQ1=sQuery(id+"F0.wireOp",EDGE,"E1.top");var subQ2=makeQuery(id+"F0.imprint","INTERSECT",VERTEX,{"disambiguationData":[OD(0.0)],"derivedFrom":[subQ1,subQ0]});Q6=makeQuery(id+"F0.imprint","IMPRINT",FACE,{"disambiguationData":[TD([[makeQuery(id+"F0.imprint","IMPRINT",EDGE,{"disambiguationData":[TD([[subQ2,-1.0]])],"derivedFrom":subQ1}),-1.0]])]});}
            var Q7;
            {var subQ15=sQuery(id+"F0.wireOp",EDGE,"E1.right");Q7=makeQuery(id+"F0.imprint","IMPRINT",FACE,{"disambiguationData":[TD([[makeQuery(id+"F0.imprint","IMPRINT",EDGE,{"derivedFrom":subQ15}),1.0]])]});}
            var Q8;
            {var subQ0=sQuery(id+"F0.wireOp",EDGE,"E15.6.4.1");var subQ1=sQuery(id+"F0.wireOp",EDGE,"E4");var subQ2=makeQuery(id+"F0.imprint","INTERSECT",VERTEX,{"disambiguationData":[OD(0.0)],"derivedFrom":[subQ1,subQ0]});Q8=makeQuery(id+"F0.imprint","IMPRINT",FACE,{"disambiguationData":[TD([[makeQuery(id+"F0.imprint","IMPRINT",EDGE,{"disambiguationData":[TD([[subQ2,-1.0]])],"derivedFrom":subQ1}),-1.0]])]});}
            var Q9;
            {var subQ0=sQuery(id+"F0.wireOp",EDGE,"E15.2.4.1");var subQ1=sQuery(id+"F0.wireOp",EDGE,"E4");var subQ2=makeQuery(id+"F0.imprint","INTERSECT",VERTEX,{"disambiguationData":[OD(0.0)],"derivedFrom":[subQ1,subQ0]});Q9=makeQuery(id+"F0.imprint","IMPRINT",FACE,{"disambiguationData":[TD([[makeQuery(id+"F0.imprint","IMPRINT",EDGE,{"disambiguationData":[TD([[subQ2,-1.0]])],"derivedFrom":subQ1}),-1.0]])]});}
            var Q10;
            {var subQ0=sQuery(id+"F0.wireOp",EDGE,"E15.6.4.2");var subQ1=sQuery(id+"F0.wireOp",EDGE,"E4");var subQ2=makeQuery(id+"F0.imprint","INTERSECT",VERTEX,{"disambiguationData":[OD(0.0)],"derivedFrom":[subQ1,subQ0]});Q10=makeQuery(id+"F0.imprint","IMPRINT",FACE,{"disambiguationData":[TD([[makeQuery(id+"F0.imprint","IMPRINT",EDGE,{"disambiguationData":[TD([[subQ2,-1.0]])],"derivedFrom":subQ1}),-1.0]])]});}
            var Q11;
            {var subQ0=sQuery(id+"F0.wireOp",EDGE,"E4");var subQ1=sQuery(id+"F0.wireOp",EDGE,"E1.top");var subQ2=makeQuery(id+"F0.imprint","INTERSECT",VERTEX,{"derivedFrom":[subQ1,subQ0]});Q11=makeQuery(id+"F0.imprint","IMPRINT",FACE,{"disambiguationData":[TD([[makeQuery(id+"F0.imprint","IMPRINT",EDGE,{"disambiguationData":[TD([[subQ2,-1.0]])],"derivedFrom":subQ1}),-1.0]])]});}
            var Q12;
            {var subQ0=sQuery(id+"F0.wireOp",EDGE,"E15.2.4.0");var subQ1=sQuery(id+"F0.wireOp",EDGE,"E4");var subQ2=makeQuery(id+"F0.imprint","INTERSECT",VERTEX,{"disambiguationData":[OD(0.0)],"derivedFrom":[subQ1,subQ0]});Q12=makeQuery(id+"F0.imprint","IMPRINT",FACE,{"disambiguationData":[TD([[makeQuery(id+"F0.imprint","IMPRINT",EDGE,{"disambiguationData":[TD([[subQ2,-1.0]])],"derivedFrom":subQ1}),-1.0]])]});}
            var Q13;
            {var subQ0=sQuery(id+"F0.wireOp",EDGE,"E15.6.4.0");var subQ1=sQuery(id+"F0.wireOp",EDGE,"E4");var subQ2=makeQuery(id+"F0.imprint","INTERSECT",VERTEX,{"disambiguationData":[OD(0.0)],"derivedFrom":[subQ1,subQ0]});Q13=makeQuery(id+"F0.imprint","IMPRINT",FACE,{"disambiguationData":[TD([[makeQuery(id+"F0.imprint","IMPRINT",EDGE,{"disambiguationData":[TD([[subQ2,-1.0]])],"derivedFrom":subQ1}),-1.0]])]});}
            var Q14;
            {var subQ0=sQuery(id+"F0.wireOp",EDGE,"E10.0.1.0");var subQ1=sQuery(id+"F0.wireOp",EDGE,"E2");var subQ2=makeQuery(id+"F0.imprint","INTERSECT",VERTEX,{"disambiguationData":[OD(0.0)],"derivedFrom":[subQ1,subQ0]});Q14=makeQuery(id+"F0.imprint","IMPRINT",FACE,{"disambiguationData":[TD([[makeQuery(id+"F0.imprint","IMPRINT",EDGE,{"disambiguationData":[TD([[subQ2,-1.0]])],"derivedFrom":subQ1}),1.0]])]});}
            extrude(context, id + "F2", {"entities" : qUnion([Q0, Q1, Q2, Q3, Q4, Q5, Q6, Q7, Q8, Q9, Q10, Q11, Q12, Q13, Q14]), "depth" : 0.3 * mm, "offsetDistance" : 25.4 * mm});
        }
        {
            var Q0;
            Q0=makeQuery(id+"F2.opExtrude","SWEPT_BODY",BODY,{"disambiguationData":[OSD([sQuery(id+"F0.wireOp",EDGE,"E1.top"),sQuery(id+"F0.wireOp",EDGE,"E10.1.2.1")])]});
            deleteBodies(context, id + "F3", {"entities" : qUnion([Q0])});
        }
    });
